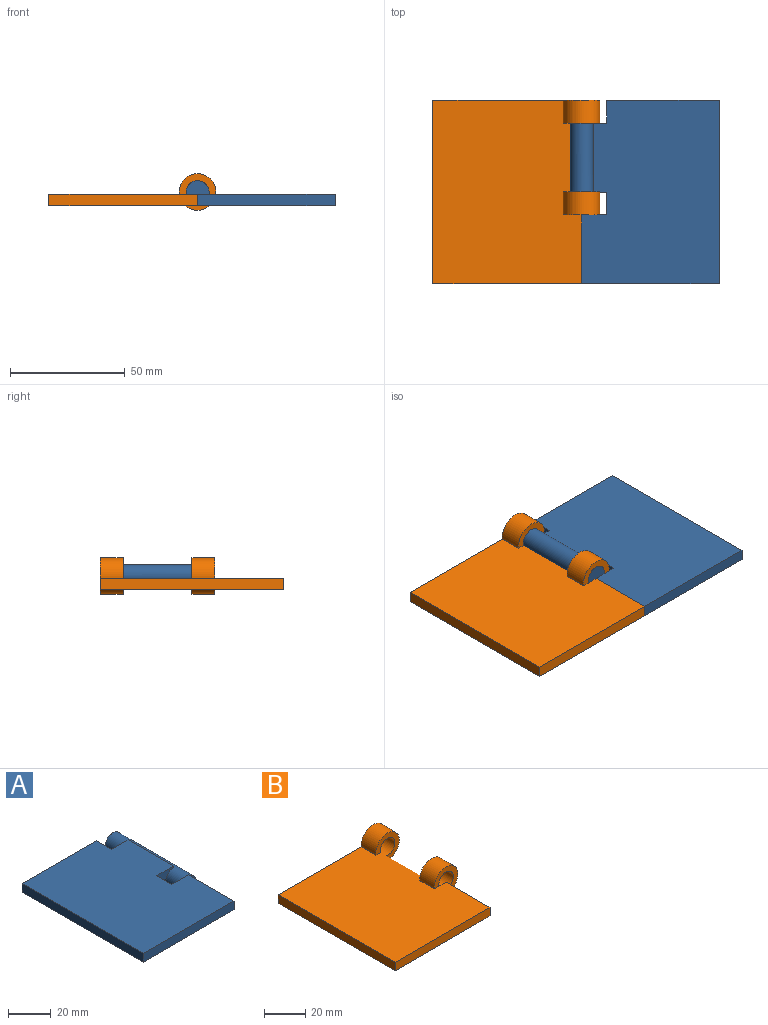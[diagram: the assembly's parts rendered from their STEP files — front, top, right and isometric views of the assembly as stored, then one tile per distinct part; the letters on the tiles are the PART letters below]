
ASSEMBLY  parts=2 mates=1
PART A: 15 faces, bbox 65x80x11 mm
  f0: plane 11x5mm, normal (0,1,0), area 40.3mm2, adj f2,f7,f8,f11,f13
  f1: plane 30x1mm, normal (1,0,0), area 30mm2, adj f9,f10,f11,f13
  f2: plane 80x60mm, normal (0,0,-1), area 4433mm2, adj f0,f3,f4,f5,f6,f7,f8,f9
  f3: plane 10x5mm, normal (1,0,0), area 50mm2, adj f2,f4,f10,f11
  f4: plane 49x5mm, normal (0,1,0), area 245mm2, adj f2,f3,f5,f11
  f5: plane 80x5mm, normal (-1,0,0), area 400mm2, adj f2,f4,f6,f11
  f6: plane 60x5mm, normal (0,-1,0), area 300mm2, adj f2,f5,f7,f11
  f7: plane 30x5mm, normal (1,0,0), area 150mm2, adj f0,f2,f6,f11,f12
  f8: plane 10x5mm, normal (1,0,0), area 50mm2, adj f0,f2,f9,f11
  f9: plane 11x5mm, normal (0,-1,0), area 40.3mm2, adj f1,f2,f8,f11,f13
  f10: plane 11x5mm, normal (0,1,0), area 40.3mm2, adj f1,f2,f3,f11,f13
  f11: plane 80x60mm, normal (0,0,1), area 4580mm2, adj f0,f1,f3,f4,f5,f6,f7,f8
  f12: plane 10x10mm, normal (0,-1,0), area 63.9mm2, adj f2,f7,f13
  f13: cylinder r=5mm len=50mm, axis (0,1,0), area 1365.4mm2, adj f0,f1,f2,f9,f10,f12,f14
  f14: plane 10x10mm, normal (0,1,0), area 78.5mm2, adj f13
PART B: 15 faces, bbox 72.9x80x16 mm
  f0: plane 16x16mm, normal (0,-1,0), area 102.2mm2, adj f1,f3,f5,f6,f11
  f1: cylinder r=8mm len=16mm, axis (0,1,0), area 444.8mm2, adj f0,f2,f5,f6
  f2: plane 16x16mm, normal (0,1,0), area 112mm2, adj f1,f3,f4,f5,f6
  f3: cylinder r=5mm len=10mm, axis (0,1,0), area 314.2mm2, adj f0,f2,f10
  f4: plane 30x5mm, normal (1,0,0), area 150mm2, adj f2,f5,f6,f12
  f5: plane 80x64.9mm, normal (0,0,1), area 4886.2mm2, adj f0,f1,f2,f4,f7,f8,f9,f10
  f6: plane 80x64.9mm, normal (0,0,-1), area 4939.1mm2, adj f0,f1,f2,f4,f7,f8,f9,f11
  f7: plane 80x5mm, normal (-1,0,0), area 400mm2, adj f5,f6,f8,f9
  f8: plane 64.9x5mm, normal (0,-1,0), area 324.5mm2, adj f5,f6,f7,f11
  f9: plane 72.9x16mm, normal (0,1,0), area 412mm2, adj f5,f6,f7,f13,f14
  f10: plane 4.9x4mm, normal (0,1,0), area 14.7mm2, adj f3,f5,f11
  f11: plane 30x5mm, normal (1,0,0), area 150mm2, adj f0,f5,f6,f8,f10
  f12: plane 16x16mm, normal (0,-1,0), area 112mm2, adj f4,f5,f6,f13,f14
  f13: cylinder r=8mm len=16mm, axis (0,-1,0), area 444.8mm2, adj f5,f6,f9,f12
  f14: cylinder r=5mm len=10mm, axis (0,-1,0), area 314.2mm2, adj f9,f12
PLACE A rot(axis=(0,-1,0),180deg) t=(0,-80,-6)mm
PLACE B t=(0,-40,0)mm
MATE revolute B.f3 <-> A.f13  axis (0,1,0) through (0,0,0)mm
